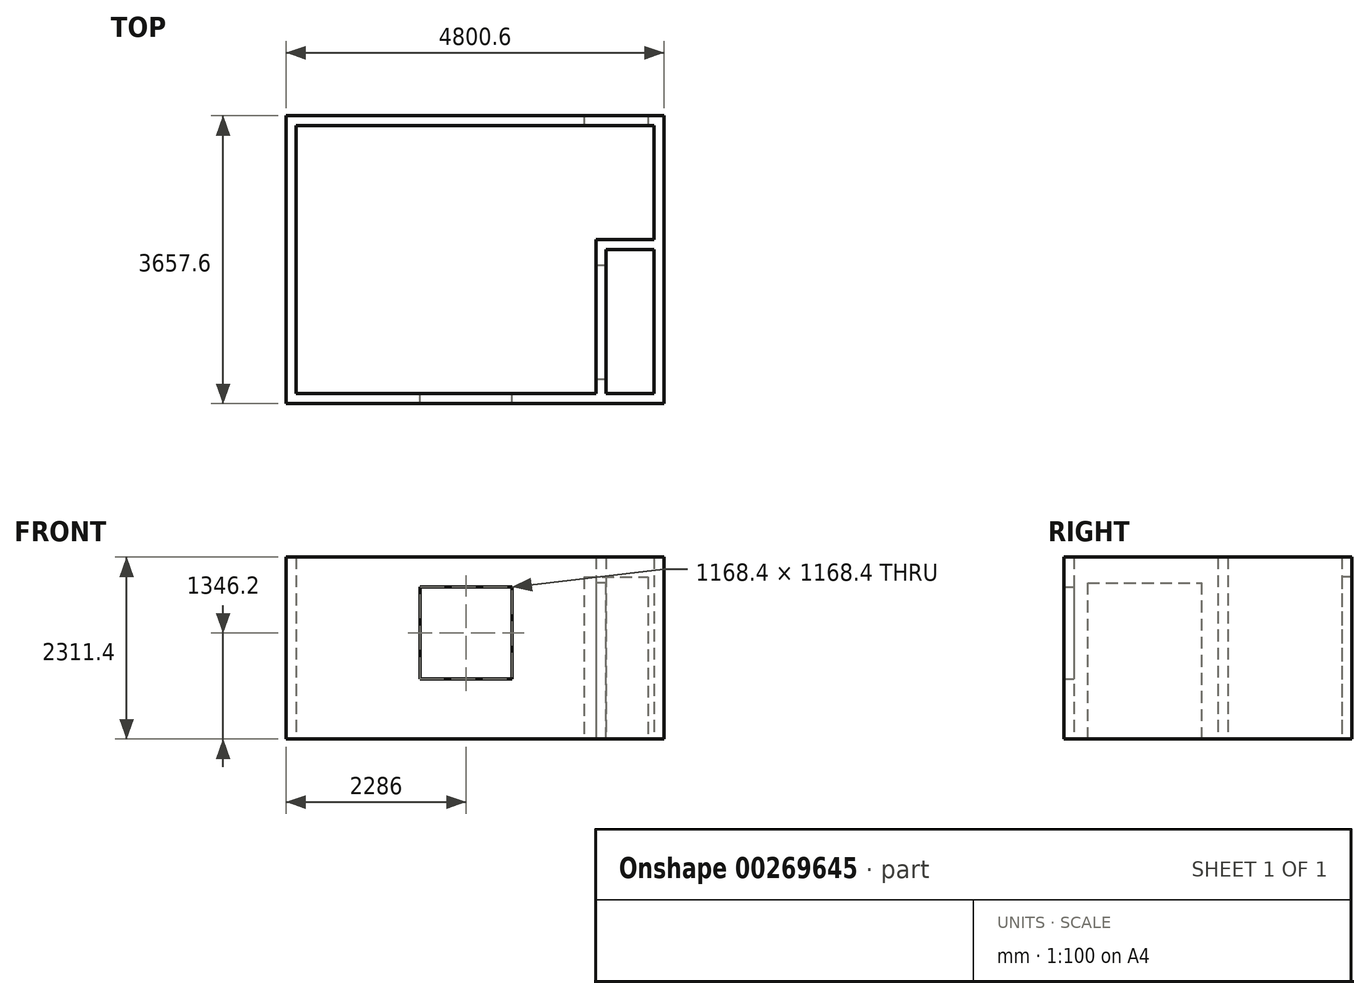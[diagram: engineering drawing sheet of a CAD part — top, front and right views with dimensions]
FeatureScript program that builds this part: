
annotation { "Feature Type Name" : "Feature", "Feature Type Description" : "" }
export const myFeature = defineFeature(function(context is Context, id is Id, definition is map)
    precondition{}
    {
        {
            var Q0;
            Q0=qCreatedBy(makeId("Top.planeOp"),FACE);
            var sketch = newSketch(context, id + "F0", { "sketchPlane" : qUnion([Q0])});
            skLineSegment(sketch, "E0.bottom", {"start": v(0, 3403.6) * mm, "end": v(4546.6, 3403.6) * mm});
            skLineSegment(sketch, "E0.top", {"start": v(0, 0) * mm, "end": v(3810, 0) * mm});
            skLineSegment(sketch, "E0.left", {"start": v(0, 3403.6) * mm, "end": v(0, 0) * mm});
            skLineSegment(sketch, "E0.right", {"start": v(4546.6, 3403.6) * mm, "end": v(4546.6, 1955.8) * mm});
            skLineSegment(sketch, "E1.bottom", {"start": v(-127, 3530.6) * mm, "end": v(4673.6, 3530.6) * mm});
            skLineSegment(sketch, "E1.top", {"start": v(-127, -127) * mm, "end": v(4673.6, -127) * mm});
            skLineSegment(sketch, "E1.left", {"start": v(-127, 3530.6) * mm, "end": v(-127, -127) * mm});
            skLineSegment(sketch, "E1.right", {"start": v(4673.6, 3530.6) * mm, "end": v(4673.6, -127) * mm});
            skLineSegment(sketch, "E2", {"start": v(3937, 0) * mm, "end": v(3937, 1828.8) * mm});
            skLineSegment(sketch, "E3", {"start": v(3937, 1828.8) * mm, "end": v(4546.6, 1828.8) * mm});
            skLineSegment(sketch, "E4", {"start": v(3810, 0) * mm, "end": v(3810, 1955.8) * mm});
            skLineSegment(sketch, "E5", {"start": v(3810, 1955.8) * mm, "end": v(4546.6, 1955.8) * mm});
            skLineSegment(sketch, "E6", {"start": v(4546.6, 1828.8) * mm, "end": v(4546.6, 0) * mm});
            skLineSegment(sketch, "E7", {"start": v(3937, 0) * mm, "end": v(4546.6, 0) * mm});
            skSolve(sketch);
        }
        {
            var Q0;
            Q0 = qSketchRegion(id + "F0", true);
            var Q1;
            Q1 = qConstructionFilter(qBodyType(qCreatedBy(id + "F0" ,EDGE), BodyType.WIRE), ConstructionObject.NO);
            extrude(context, id + "F1", {"entities" : qUnion([Q0]), "surfaceEntities" : qUnion([Q1]), "depth" : 2311.4 * mm});
        }
        {
            var Q0;
            Q0=makeQuery(id+"F1.opExtrude","SWEPT_FACE",FACE,{"disambiguationData":[OSD([sQuery(id+"F0.wireOp",EDGE,"E0.top")])]});
            var sketch = newSketch(context, id + "F2", { "sketchPlane" : qUnion([Q0])});
            skLineSegment(sketch, "E8.bottom", {"start": v(-1574.8, 762) * mm, "end": v(-2743.2, 762) * mm});
            skLineSegment(sketch, "E8.top", {"start": v(-1574.8, 1930.4) * mm, "end": v(-2743.2, 1930.4) * mm});
            skLineSegment(sketch, "E8.left", {"start": v(-2743.2, 1930.4) * mm, "end": v(-2743.2, 762) * mm});
            skLineSegment(sketch, "E8.right", {"start": v(-1574.8, 1930.4) * mm, "end": v(-1574.8, 762) * mm});
            skSolve(sketch);
        }
        {
            var Q0;
            Q0 = qSketchRegion(id + "F2", true);
            var Q1;
            Q1 = qConstructionFilter(qBodyType(qCreatedBy(id + "F2" ,EDGE), BodyType.WIRE), ConstructionObject.NO);
            var Q2;
            Q2=makeQuery(id+"F1.opExtrude","SWEPT_FACE",FACE,{"disambiguationData":[OSD([sQuery(id+"F0.wireOp",EDGE,"E0.top")])]});
            extrude(context, id + "F3", {"entities" : qUnion([Q0]), "operationType" : NewBodyOperationType.REMOVE, "surfaceEntities" : qUnion([Q1]), "endBound" : BoundingType.UP_TO_NEXT, "oppositeDirection" : true, "endBoundEntityFace" : qUnion([Q2]), "depth" : 101.6 * mm});
        }
        {
            var Q0;
            Q0=makeQuery(id+"F1.opExtrude","SWEPT_FACE",FACE,{"disambiguationData":[OSD([sQuery(id+"F0.wireOp",EDGE,"E0.bottom")])]});
            var sketch = newSketch(context, id + "F4", { "sketchPlane" : qUnion([Q0])});
            skLineSegment(sketch, "E9.bottom", {"start": v(3657.6, 2057.4) * mm, "end": v(4470.4, 2057.4) * mm});
            skLineSegment(sketch, "E9.top", {"start": v(3657.6, 0) * mm, "end": v(4470.4, 0) * mm});
            skLineSegment(sketch, "E9.left", {"start": v(3657.6, 2057.4) * mm, "end": v(3657.6, 0) * mm});
            skLineSegment(sketch, "E9.right", {"start": v(4470.4, 2057.4) * mm, "end": v(4470.4, 0) * mm});
            skSolve(sketch);
        }
        {
            var Q0;
            Q0 = qSketchRegion(id + "F4", true);
            extrude(context, id + "F5", {"entities" : qUnion([Q0]), "operationType" : NewBodyOperationType.REMOVE, "endBound" : BoundingType.UP_TO_NEXT, "oppositeDirection" : true, "depth" : 25.4 * mm});
        }
        {
            var Q0;
            Q0=makeQuery(id+"F1.opExtrude","SWEPT_FACE",FACE,{"disambiguationData":[OSD([sQuery(id+"F0.wireOp",EDGE,"E4")])]});
            var sketch = newSketch(context, id + "F6", { "sketchPlane" : qUnion([Q0])});
            skLineSegment(sketch, "E10.bottom", {"start": v(-1625.6, 1981.2) * mm, "end": v(-177.8, 1981.2) * mm});
            skLineSegment(sketch, "E10.top", {"start": v(-1625.6, 0) * mm, "end": v(-177.8, 0) * mm});
            skLineSegment(sketch, "E10.left", {"start": v(-1625.6, 1981.2) * mm, "end": v(-1625.6, 0) * mm});
            skLineSegment(sketch, "E10.right", {"start": v(-177.8, 1981.2) * mm, "end": v(-177.8, 0) * mm});
            skSolve(sketch);
        }
        {
            var Q0;
            Q0=makeQuery(id+"F6.imprint","IMPRINT",FACE,{"disambiguationData":[TD([[makeQuery(id+"F6.imprint","IMPRINT",EDGE,{"derivedFrom":sQuery(id+"F6.wireOp",EDGE,"E10.bottom")}),-1.0]])]});
            extrude(context, id + "F7", {"entities" : qUnion([Q0]), "operationType" : NewBodyOperationType.REMOVE, "endBound" : BoundingType.UP_TO_NEXT, "oppositeDirection" : true, "depth" : 25.4 * mm});
        }
    });
